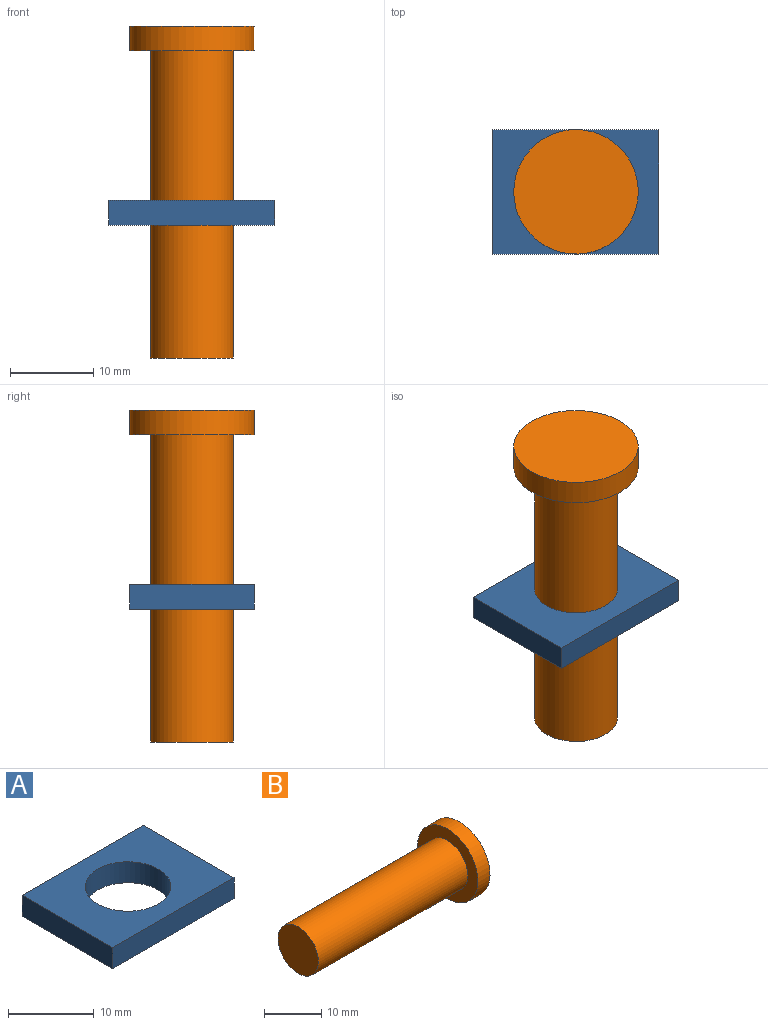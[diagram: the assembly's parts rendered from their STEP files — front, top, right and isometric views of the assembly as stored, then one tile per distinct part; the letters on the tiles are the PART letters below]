
ASSEMBLY  parts=2 mates=1
PART A: 7 faces, bbox 20x15x3 mm
  f0: plane 15x3mm, normal (-1,0,0), area 45mm2, adj f1,f3,f5,f6
  f1: plane 20x3mm, normal (0,-1,0), area 60mm2, adj f0,f2,f5,f6
  f2: plane 15x3mm, normal (1,0,0), area 45mm2, adj f1,f3,f5,f6
  f3: plane 20x3mm, normal (0,1,0), area 60mm2, adj f0,f2,f5,f6
  f4: cylinder r=5mm len=10mm, axis (0,0,-1), area 94.2mm2, adj f5,f6
  f5: plane 20x15mm, normal (0,0,1), area 221.5mm2, adj f0,f1,f2,f3,f4
  f6: plane 20x15mm, normal (0,0,-1), area 221.5mm2, adj f0,f1,f2,f3,f4
PART B: 5 faces, bbox 40x15x15 mm
  f0: plane 15x15mm, normal (1,0,0), area 176.7mm2, adj f1
  f1: cylinder r=7.5mm len=15mm, axis (-1,0,0), area 141.4mm2, adj f0,f2
  f2: plane 15x15mm, normal (-1,0,0), area 98.2mm2, adj f1,f3
  f3: cylinder r=5mm len=37mm, axis (-1,0,0), area 1162.4mm2, adj f2,f4
  f4: plane 10x10mm, normal (-1,0,0), area 78.5mm2, adj f3
PLACE A t=(-2.94,46.55,6.52)mm
PLACE B rot(axis=(0,-1,0),90deg) t=(-2.94,46.55,26.02)mm
MATE fastened B.f1 <-> A.f4  axis (0,0,-1) through (-2.94,46.55,-10.98)mm
